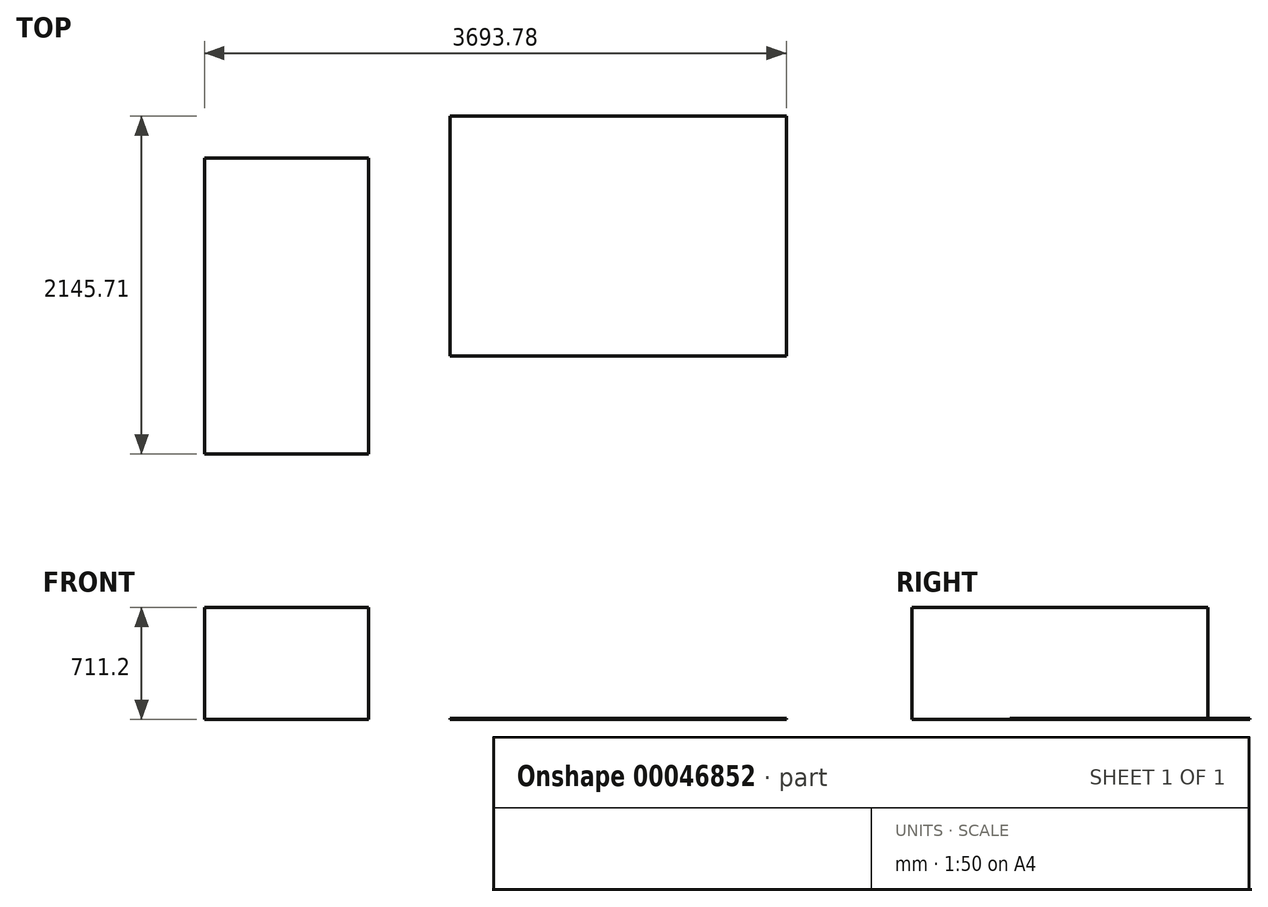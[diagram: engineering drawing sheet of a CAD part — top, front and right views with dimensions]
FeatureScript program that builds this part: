
annotation { "Feature Type Name" : "Feature", "Feature Type Description" : "" }
export const myFeature = defineFeature(function(context is Context, id is Id, definition is map)
    precondition{}
    {
        {
            var Q0;
            Q0=qCreatedBy(makeId("Top.planeOp"),FACE);
            var sketch = newSketch(context, id + "F0", { "sketchPlane" : qUnion([Q0])});
            skLineSegment(sketch, "E0.bottom", {"start": v(0, 0) * mm, "end": v(1041.4, 0) * mm});
            skLineSegment(sketch, "E0.top", {"start": v(0, -1879.6) * mm, "end": v(1041.4, -1879.6) * mm});
            skLineSegment(sketch, "E0.left", {"start": v(0, 0) * mm, "end": v(0, -1879.6) * mm});
            skLineSegment(sketch, "E0.right", {"start": v(1041.4, 0) * mm, "end": v(1041.4, -1879.6) * mm});
            skSolve(sketch);
        }
        {
            var Q0;
            Q0=qSketchRegion(id+"F0",true);
            extrude(context, id + "F1", {"entities" : qUnion([Q0]), "depth" : 711.2 * mm});
        }
        {
            var Q0;
            Q0=qCreatedBy(makeId("Top.planeOp"),FACE);
            var sketch = newSketch(context, id + "F2", { "sketchPlane" : qUnion([Q0])});
            skLineSegment(sketch, "E1.bottom", {"start": v(1560.18, 266.11) * mm, "end": v(3693.78, 266.11) * mm});
            skLineSegment(sketch, "E1.top", {"start": v(1560.18, -1257.89) * mm, "end": v(3693.78, -1257.89) * mm});
            skLineSegment(sketch, "E1.left", {"start": v(1560.18, 266.11) * mm, "end": v(1560.18, -1257.89) * mm});
            skLineSegment(sketch, "E1.right", {"start": v(3693.78, 266.11) * mm, "end": v(3693.78, -1257.89) * mm});
            skSolve(sketch);
        }
        {
            var Q0;
            Q0=qSketchRegion(id+"F2",true);
            extrude(context, id + "F3", {"entities" : qUnion([Q0]), "depth" : 6.35 * mm});
        }
    });
